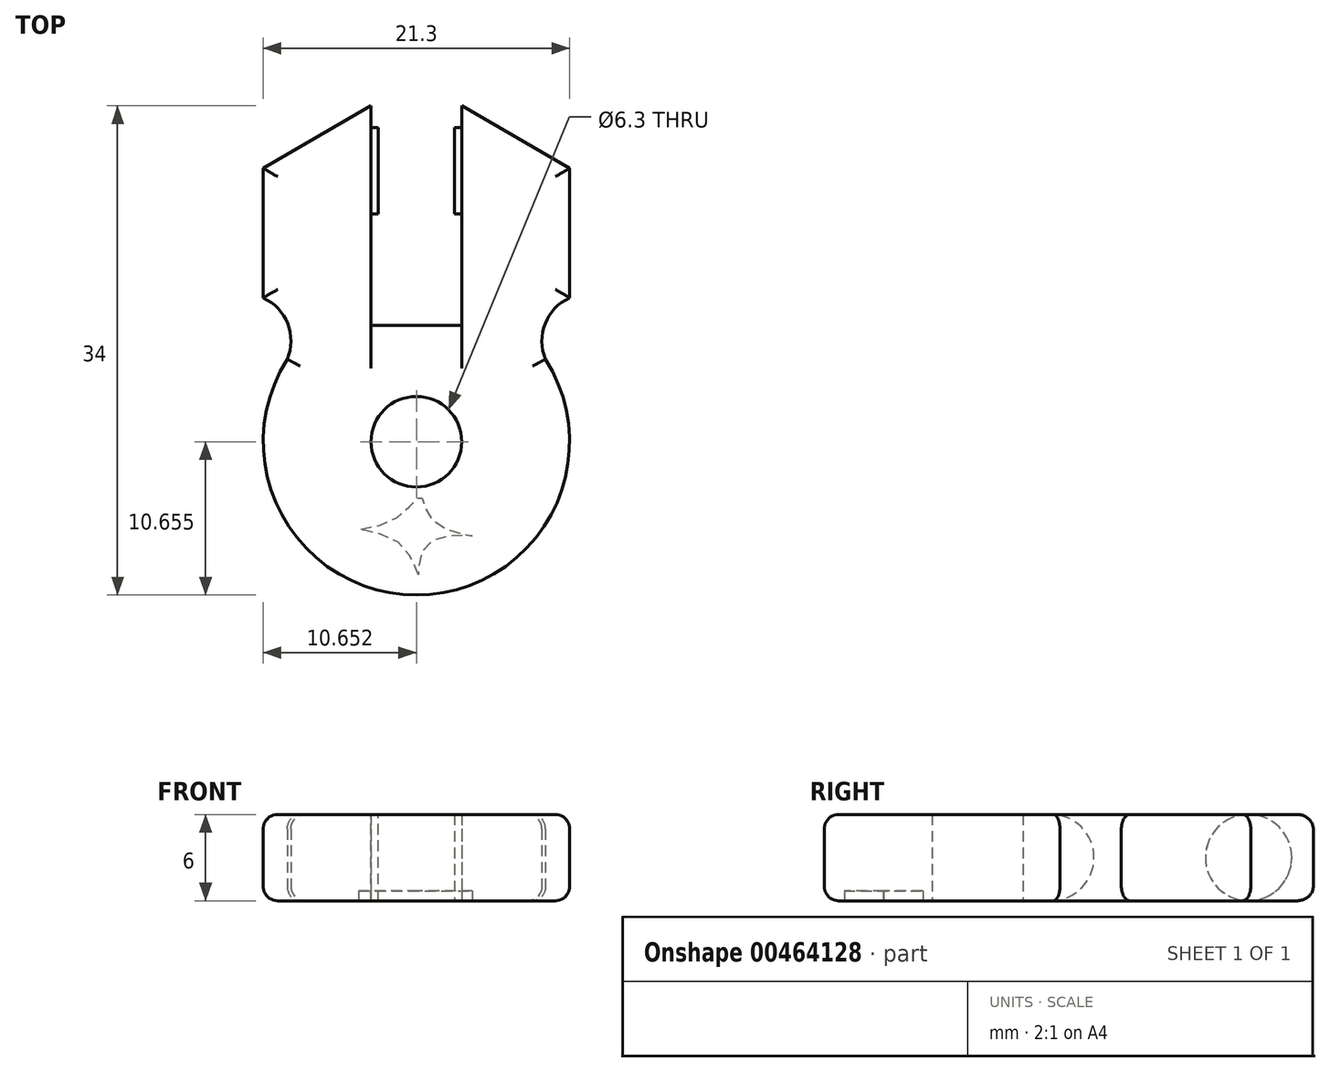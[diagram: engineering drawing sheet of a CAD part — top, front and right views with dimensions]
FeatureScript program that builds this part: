
annotation { "Feature Type Name" : "Feature", "Feature Type Description" : "" }
export const myFeature = defineFeature(function(context is Context, id is Id, definition is map)
    precondition{}
    {
        {
            var Q0;
            Q0=qCreatedBy(makeId("Top.planeOp"),FACE);
            var sketch = newSketch(context, id + "F0", { "sketchPlane" : qUnion([Q0])});
            skArc(sketch, "E0", {"start": v(-48.37, 35.67) * mm, "mid": v(-45.22, 14.84) * mm, "end": v(-42.07, 35.67) * mm});
            skCircle(sketch, "E1", {"center": v(-45.22, 25.5) * mm, "radius": 3.15 * mm});
            skLineSegment(sketch, "E2", {"start": v(-32.24, 25.5) * mm, "end": v(-32.24, 33.6) * mm});
            skPoint(sketch, "E3", {"position": v(-45.22, 33.6) * mm});
            skLineSegment(sketch, "E4", {"start": v(-48.37, 33.6) * mm, "end": v(-48.37, 48.84) * mm});
            skLineSegment(sketch, "E5", {"start": v(-48.37, 48.84) * mm, "end": v(-48.37, 44.5) * mm});
            skPoint(sketch, "E6", {"position": v(-55.87, 44.5) * mm});
            skLineSegment(sketch, "E7", {"start": v(-55.87, 44.5) * mm, "end": v(-48.37, 48.84) * mm});
            skPoint(sketch, "E8.end.orphan", {"position": v(-55.87, 48.84) * mm});
            skLineSegment(sketch, "E9", {"start": v(-55.87, 44.5) * mm, "end": v(-55.87, 35.5) * mm});
            skArc(sketch, "E10", {"start": v(-54.64, 30.46) * mm, "mid": v(-54.04, 33.28) * mm, "end": v(-55.87, 35.5) * mm});
            skArc(sketch, "E11.MirrorCS", {"start": v(-35.8, 30.46) * mm, "mid": v(-36.4, 33.28) * mm, "end": v(-34.57, 35.5) * mm});
            skLineSegment(sketch, "E12.MirrorCS", {"start": v(-42.07, 33.6) * mm, "end": v(-42.07, 48.84) * mm});
            skLineSegment(sketch, "E13.MirrorCS", {"start": v(-34.57, 44.5) * mm, "end": v(-34.57, 35.5) * mm});
            skLineSegment(sketch, "E14.MirrorCS", {"start": v(-34.57, 44.5) * mm, "end": v(-42.07, 48.84) * mm});
            skPoint(sketch, "E15.orphan", {"position": v(-35.8, 30.46) * mm});
            skLineSegment(sketch, "E16", {"start": v(-45.22, 30.6) * mm, "end": v(-42.07, 30.6) * mm});
            skLineSegment(sketch, "E17", {"start": v(-42.07, 30.6) * mm, "end": v(-48.37, 30.6) * mm});
            skPoint(sketch, "E18.end.orphan", {"position": v(-42.07, 33.6) * mm});
            skLineSegment(sketch, "E19", {"start": v(-42.07, 33.6) * mm, "end": v(-42.07, 30.6) * mm});
            skLineSegment(sketch, "E20", {"start": v(-48.37, 33.6) * mm, "end": v(-48.37, 30.6) * mm});
            skSolve(sketch);
        }
        {
            var Q0;
            Q0 = qSketchRegion(id + "F0", true);
            extrude(context, id + "F1", {"entities" : qUnion([Q0]), "depth" : 6 * mm});
        }
        {
            var Q0;
            Q0=makeQuery(id+"F1.opExtrude","SWEPT_FACE",FACE,{"disambiguationData":[OSD([sQuery(id+"F0.wireOp",EDGE,"E12.MirrorCS")])]});
            var sketch = newSketch(context, id + "F2", { "sketchPlane" : qUnion([Q0])});
            skLineSegment(sketch, "E21", {"start": v(-48.84, 3) * mm, "end": v(-47.34, 3) * mm});
            skPoint(sketch, "E21.endSnap0", {"position": v(-48.84, 3) * mm});
            skCircle(sketch, "E22", {"center": v(-44.34, 3) * mm, "radius": 3 * mm});
            skArc(sketch, "E23", {"start": v(-48.84, 6) * mm, "mid": v(-51.84, 3) * mm, "end": v(-48.84, 0) * mm});
            skArc(sketch, "E24", {"start": v(-30.6, 6) * mm, "mid": v(-33.6, 3) * mm, "end": v(-30.6, 0) * mm});
            skSolve(sketch);
        }
        {
            var Q0;
            {var subQ0=sQuery(id+"F2.wireOp",EDGE,"E22");var subQ1=makeQuery(id+"F2.imprint","INTERSECT",VERTEX,{"derivedFrom":[sQuery(id+"F2.wireOp",EDGE,"E21"),subQ0]});Q0=makeQuery(id+"F2.imprint","IMPRINT",FACE,{"disambiguationData":[TD([[makeQuery(id+"F2.imprint","IMPRINT",EDGE,{"disambiguationData":[TD([[subQ1,1.0]])],"derivedFrom":subQ0}),1.0]])]});}
            extrude(context, id + "F3", {"entities" : qUnion([Q0]), "operationType" : NewBodyOperationType.ADD, "depth" : .5 * mm});
        }
        {
            var Q0;
            Q0=makeQuery(id+"F1.opExtrude","SWEPT_FACE",FACE,{"disambiguationData":[OSD([sQuery(id+"F0.wireOp",EDGE,"E4"),sQuery(id+"F0.wireOp",EDGE,"E5")])]});
            var sketch = newSketch(context, id + "F4", { "sketchPlane" : qUnion([Q0])});
            skLineSegment(sketch, "E25", {"start": v(48.84, 3) * mm, "end": v(47.34, 3) * mm});
            skCircle(sketch, "E26", {"center": v(44.34, 3) * mm, "radius": 3 * mm});
            skSolve(sketch);
        }
        {
            var Q0;
            {var subQ0=sQuery(id+"F4.wireOp",EDGE,"E26");var subQ1=makeQuery(id+"F4.imprint","INTERSECT",VERTEX,{"derivedFrom":[sQuery(id+"F4.wireOp",EDGE,"E25"),subQ0]});Q0=makeQuery(id+"F4.imprint","IMPRINT",FACE,{"disambiguationData":[TD([[makeQuery(id+"F4.imprint","IMPRINT",EDGE,{"disambiguationData":[TD([[subQ1,-1.0]])],"derivedFrom":subQ0}),1.0]])]});}
            extrude(context, id + "F5", {"entities" : qUnion([Q0]), "operationType" : NewBodyOperationType.ADD, "depth" : .5 * mm});
        }
        {
            var Q0;
            Q0=makeQuery(id+"F2.imprint","IMPRINT",FACE,{"disambiguationData":[TD([[makeQuery(id+"F2.imprint","IMPRINT",EDGE,{"derivedFrom":sQuery(id+"F2.wireOp",EDGE,"E24")}),1.0]])]});
            extrude(context, id + "F6", {"entities" : qUnion([Q0]), "operationType" : NewBodyOperationType.ADD, "depth" : 9.1 * mm});
        }
        {
            var Q0;
            Q0=makeQuery(id+"F1.opExtrude","CAP_EDGE",EDGE,{"disambiguationData":[OSD([sQuery(id+"F0.wireOp",EDGE,"E7")])],"isStart":false});
            var Q1;
            Q1=makeQuery(id+"F1.opExtrude","CAP_EDGE",EDGE,{"disambiguationData":[OSD([sQuery(id+"F0.wireOp",EDGE,"E9")])],"isStart":false});
            var Q2;
            Q2=makeQuery(id+"F1.opExtrude","CAP_EDGE",EDGE,{"disambiguationData":[OSD([sQuery(id+"F0.wireOp",EDGE,"E10")])],"isStart":false});
            var Q3;
            Q3=makeQuery(id+"F1.opExtrude","CAP_EDGE",EDGE,{"disambiguationData":[OSD([sQuery(id+"F0.wireOp",EDGE,"E0")])],"isStart":false});
            var Q4;
            Q4=makeQuery(id+"F1.opExtrude","CAP_EDGE",EDGE,{"disambiguationData":[OSD([sQuery(id+"F0.wireOp",EDGE,"E11.MirrorCS")])],"isStart":false});
            var Q5;
            Q5=makeQuery(id+"F1.opExtrude","CAP_EDGE",EDGE,{"disambiguationData":[OSD([sQuery(id+"F0.wireOp",EDGE,"E13.MirrorCS")])],"isStart":false});
            var Q6;
            Q6=makeQuery(id+"F1.opExtrude","CAP_EDGE",EDGE,{"disambiguationData":[OSD([sQuery(id+"F0.wireOp",EDGE,"E14.MirrorCS")])],"isStart":false});
            fillet(context, id + "F7", {"entities" : qUnion([Q0, Q1, Q2, Q3, Q4, Q5, Q6]), "radius" : 1 * mm, "tangentPropagation" : true, "allowEdgeOverflow" : false});
        }
        {
            var Q0;
            Q0=makeQuery(id+"F1.opExtrude","CAP_EDGE",EDGE,{"disambiguationData":[OSD([sQuery(id+"F0.wireOp",EDGE,"E14.MirrorCS")])],"isStart":true});
            var Q1;
            Q1=makeQuery(id+"F1.opExtrude","CAP_EDGE",EDGE,{"disambiguationData":[OSD([sQuery(id+"F0.wireOp",EDGE,"E13.MirrorCS")])],"isStart":true});
            var Q2;
            Q2=makeQuery(id+"F1.opExtrude","CAP_EDGE",EDGE,{"disambiguationData":[OSD([sQuery(id+"F0.wireOp",EDGE,"E11.MirrorCS")])],"isStart":true});
            var Q3;
            Q3=makeQuery(id+"F1.opExtrude","CAP_EDGE",EDGE,{"disambiguationData":[OSD([sQuery(id+"F0.wireOp",EDGE,"E0")])],"isStart":true});
            var Q4;
            Q4=makeQuery(id+"F1.opExtrude","CAP_EDGE",EDGE,{"disambiguationData":[OSD([sQuery(id+"F0.wireOp",EDGE,"E10")])],"isStart":true});
            var Q5;
            Q5=makeQuery(id+"F1.opExtrude","CAP_EDGE",EDGE,{"disambiguationData":[OSD([sQuery(id+"F0.wireOp",EDGE,"E9")])],"isStart":true});
            var Q6;
            Q6=makeQuery(id+"F1.opExtrude","CAP_EDGE",EDGE,{"disambiguationData":[OSD([sQuery(id+"F0.wireOp",EDGE,"E7")])],"isStart":true});
            fillet(context, id + "F8", {"entities" : qUnion([Q0, Q1, Q2, Q3, Q4, Q5, Q6]), "radius" : 1 * mm, "tangentPropagation" : true, "allowEdgeOverflow" : false});
        }
        {
            var Q0;
            Q0=makeQuery(id+"F1.opExtrude","CAP_FACE",FACE,{"disambiguationData":[OSD([sQuery(id+"F0.wireOp",EDGE,"E0"),sQuery(id+"F0.wireOp",EDGE,"E1"),sQuery(id+"F0.wireOp",EDGE,"E4"),sQuery(id+"F0.wireOp",EDGE,"E5"),sQuery(id+"F0.wireOp",EDGE,"E7"),sQuery(id+"F0.wireOp",EDGE,"E9"),sQuery(id+"F0.wireOp",EDGE,"E10"),sQuery(id+"F0.wireOp",EDGE,"E11.MirrorCS"),sQuery(id+"F0.wireOp",EDGE,"E12.MirrorCS"),sQuery(id+"F0.wireOp",EDGE,"E13.MirrorCS"),sQuery(id+"F0.wireOp",EDGE,"E14.MirrorCS"),sQuery(id+"F0.wireOp",EDGE,"E17"),sQuery(id+"F0.wireOp",EDGE,"E19"),sQuery(id+"F0.wireOp",EDGE,"E20")])],"isStart":true});
            var sketch = newSketch(context, id + "F9", { "sketchPlane" : qUnion([Q0])});
            skFitSpline(sketch, "E27", {"points": [v(-45.09, -16.24) * mm, v(-46.3, -18.36) * mm, v(-49.23, -19.4) * mm, v(-46.79, -20.08) * mm, v(-44.9, -21.7) * mm, v(-44.1, -20.02) * mm, v(-41.33, -18.95) * mm, v(-44.43, -18.42) * mm, v(-45.09, -16.24) * mm]});
            skSolve(sketch);
        }
        {
            var Q0;
            Q0 = qSketchRegion(id + "F9", true);
            extrude(context, id + "F10", {"entities" : qUnion([Q0]), "operationType" : NewBodyOperationType.REMOVE, "oppositeDirection" : true, "depth" : 0.7 * mm});
        }
    });
